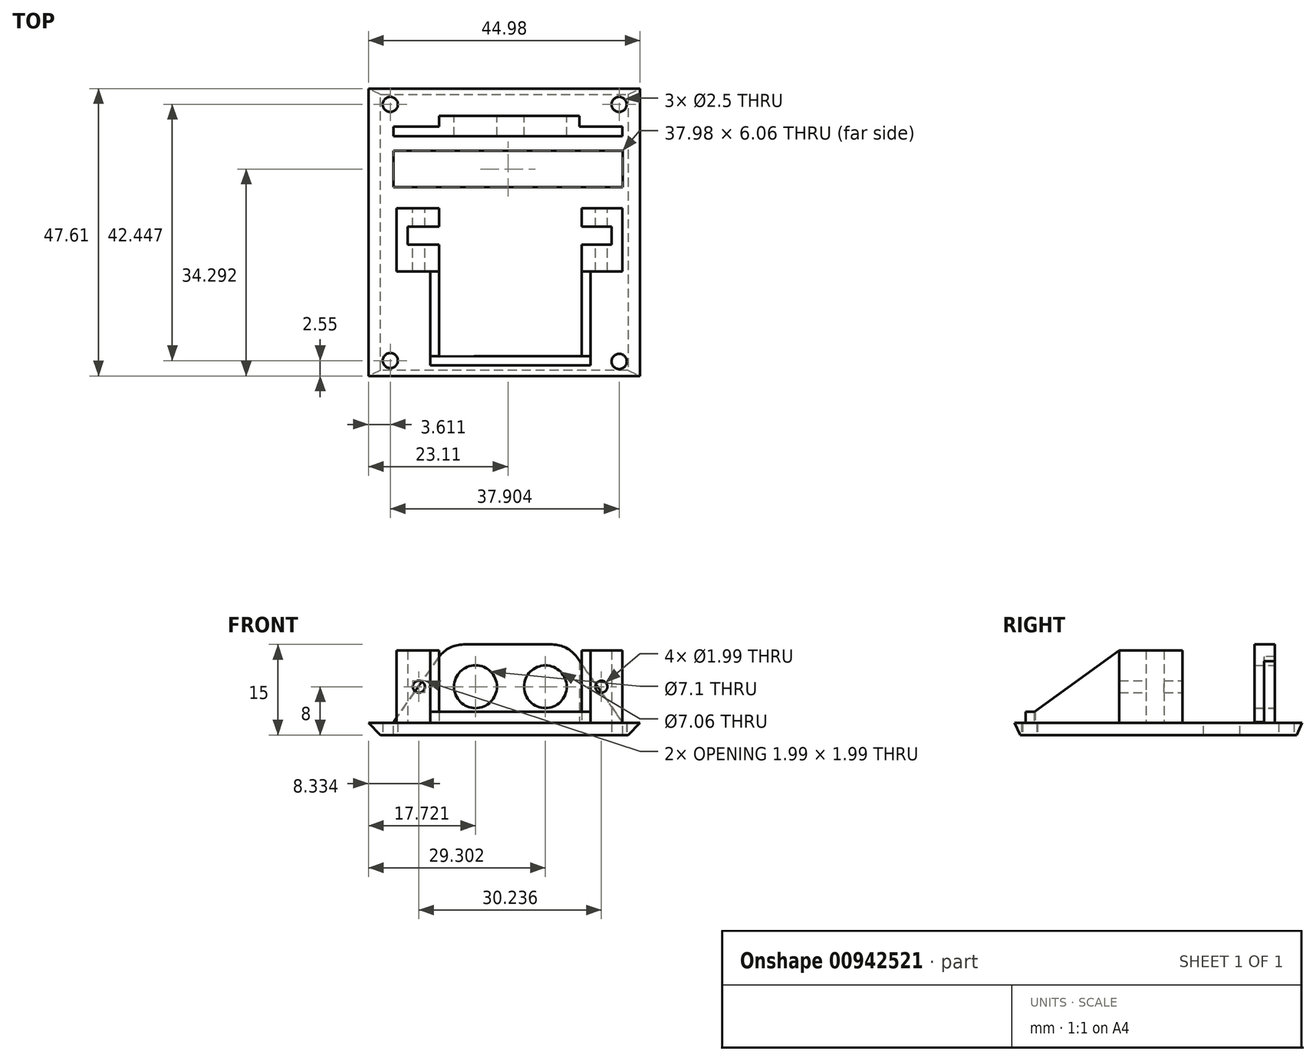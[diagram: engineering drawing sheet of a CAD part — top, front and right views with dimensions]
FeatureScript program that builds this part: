
annotation { "Feature Type Name" : "Feature", "Feature Type Description" : "" }
export const myFeature = defineFeature(function(context is Context, id is Id, definition is map)
    precondition{}
    {
        {
            var Q0;
            Q0=qCreatedBy(makeId("Top.planeOp"),FACE);
            var sketch = newSketch(context, id + "F0", { "sketchPlane" : qUnion([Q0])});
            skLineSegment(sketch, "E0.bottom", {"start": v(0, 0) * mm, "end": v(-44.98, 0) * mm});
            skLineSegment(sketch, "E0.top", {"start": v(0, 49.75) * mm, "end": v(-44.98, 49.75) * mm});
            skLineSegment(sketch, "E0.left", {"start": v(0, 0) * mm, "end": v(0, 49.75) * mm});
            skLineSegment(sketch, "E0.right", {"start": v(-44.98, 0) * mm, "end": v(-44.98, 49.75) * mm});
            skSolve(sketch);
        }
        {
            var Q0;
            Q0=makeQuery(id+"F0.imprint","IMPRINT",FACE,{"disambiguationData":[TD([[makeQuery(id+"F0.imprint","IMPRINT",EDGE,{"derivedFrom":sQuery(id+"F0.wireOp",EDGE,"E0.bottom")}),-1.0]])]});
            var sketch = newSketch(context, id + "F1", { "sketchPlane" : qUnion([Q0])});
            skLineSegment(sketch, "E1", {"start": v(-9.68, 4.44) * mm, "end": v(-9.68, 22.8) * mm});
            skLineSegment(sketch, "E2", {"start": v(-9.68, 22.8) * mm, "end": v(-4.7, 22.8) * mm});
            skLineSegment(sketch, "E3", {"start": v(-4.7, 22.8) * mm, "end": v(-4.7, 25.8) * mm});
            skLineSegment(sketch, "E4", {"start": v(-4.7, 25.8) * mm, "end": v(-9.68, 25.8) * mm});
            skLineSegment(sketch, "E5", {"start": v(-9.68, 25.8) * mm, "end": v(-9.68, 28.87) * mm});
            skLineSegment(sketch, "E6", {"start": v(-9.68, 28.87) * mm, "end": v(-2.9, 28.87) * mm});
            skLineSegment(sketch, "E7", {"start": v(-2.9, 28.87) * mm, "end": v(-2.9, 18.4) * mm});
            skLineSegment(sketch, "E8", {"start": v(-2.9, 18.4) * mm, "end": v(-8.18, 18.4) * mm});
            skLineSegment(sketch, "E9", {"start": v(-8.18, 18.4) * mm, "end": v(-8.18, 2.84) * mm});
            skLineSegment(sketch, "E10", {"start": v(-8.18, 2.84) * mm, "end": v(-34.77, 2.84) * mm});
            skLineSegment(sketch, "E11", {"start": v(-34.77, 2.84) * mm, "end": v(-34.77, 18.4) * mm});
            skLineSegment(sketch, "E12", {"start": v(-34.77, 18.4) * mm, "end": v(-40.33, 18.4) * mm});
            skLineSegment(sketch, "E13", {"start": v(-40.33, 18.4) * mm, "end": v(-40.33, 28.87) * mm});
            skLineSegment(sketch, "E14", {"start": v(-40.33, 28.87) * mm, "end": v(-33.26, 28.87) * mm});
            skLineSegment(sketch, "E15", {"start": v(-33.26, 28.87) * mm, "end": v(-33.26, 25.8) * mm});
            skLineSegment(sketch, "E16", {"start": v(-33.26, 25.8) * mm, "end": v(-38.5, 25.8) * mm});
            skLineSegment(sketch, "E17", {"start": v(-38.5, 25.8) * mm, "end": v(-38.5, 22.8) * mm});
            skLineSegment(sketch, "E18", {"start": v(-38.5, 22.8) * mm, "end": v(-33.26, 22.8) * mm});
            skLineSegment(sketch, "E19", {"start": v(-33.26, 22.8) * mm, "end": v(-33.26, 4.3) * mm});
            skLineSegment(sketch, "E20", {"start": v(-33.26, 4.3) * mm, "end": v(-9.68, 4.44) * mm});
            skLineSegment(sketch, "E21", {"start": v(-40.84, 40.8) * mm, "end": v(-2.94, 40.8) * mm});
            skLineSegment(sketch, "E22", {"start": v(-2.94, 40.8) * mm, "end": v(-2.94, 42.4) * mm});
            skLineSegment(sketch, "E23", {"start": v(-2.94, 42.4) * mm, "end": v(-10.02, 42.4) * mm});
            skLineSegment(sketch, "E24", {"start": v(-10.02, 42.4) * mm, "end": v(-10.02, 44.17) * mm});
            skLineSegment(sketch, "E25", {"start": v(-10.02, 44.17) * mm, "end": v(-33.26, 44.17) * mm});
            skLineSegment(sketch, "E26", {"start": v(-33.26, 44.17) * mm, "end": v(-33.26, 42.4) * mm});
            skLineSegment(sketch, "E27", {"start": v(-33.26, 42.4) * mm, "end": v(-40.84, 42.4) * mm});
            skLineSegment(sketch, "E28", {"start": v(-40.84, 42.4) * mm, "end": v(-40.84, 40.8) * mm});
            skSolve(sketch);
        }
        {
            var Q0;
            Q0=qCreatedBy(makeId("Top.planeOp"),FACE);
            var sketch = newSketch(context, id + "F2", { "sketchPlane" : qUnion([Q0])});
            skLineSegment(sketch, "E29.bottom", {"start": v(-40.86, 38.4) * mm, "end": v(-2.88, 38.4) * mm});
            skLineSegment(sketch, "E29.top", {"start": v(-40.86, 32.33) * mm, "end": v(-2.88, 32.33) * mm});
            skLineSegment(sketch, "E29.left", {"start": v(-40.86, 38.4) * mm, "end": v(-40.86, 32.33) * mm});
            skLineSegment(sketch, "E29.right", {"start": v(-2.88, 38.4) * mm, "end": v(-2.88, 32.33) * mm});
            skSolve(sketch);
        }
        {
            var Q0;
            Q0 = qSketchRegion(id + "F0", true);
            extrude(context, id + "F3", {"entities" : qUnion([Q0]), "oppositeDirection" : true, "depth" : 2 * mm, "offsetDistance" : 25 * mm});
        }
        {
            var Q0;
            Q0=makeQuery(id+"F1.imprint","IMPRINT",FACE,{"disambiguationData":[TD([[makeQuery(id+"F1.imprint","IMPRINT",EDGE,{"derivedFrom":sQuery(id+"F1.wireOp",EDGE,"E1")}),-1.0]])]});
            extrude(context, id + "F4", {"entities" : qUnion([Q0]), "operationType" : NewBodyOperationType.ADD, "depth" : 12 * mm, "offsetDistance" : 25 * mm});
        }
        {
            var Q0;
            Q0 = qSketchRegion(id + "F2", true);
            extrude(context, id + "F5", {"entities" : qUnion([Q0]), "operationType" : NewBodyOperationType.REMOVE, "oppositeDirection" : true, "depth" : 6.6 * mm, "offsetDistance" : 25 * mm});
        }
        {
            var Q0;
            Q0=makeQuery(id+"F1.imprint","IMPRINT",FACE,{"disambiguationData":[TD([[makeQuery(id+"F1.imprint","IMPRINT",EDGE,{"derivedFrom":sQuery(id+"F1.wireOp",EDGE,"E21")}),1.0]])]});
            extrude(context, id + "F6", {"entities" : qUnion([Q0]), "operationType" : NewBodyOperationType.ADD, "depth" : 13 * mm, "offsetDistance" : 25 * mm});
        }
        {
            var Q0;
            Q0=makeQuery(id+"F6.opExtrude","SWEPT_FACE",FACE,{"disambiguationData":[OSD([sQuery(id+"F1.wireOp",EDGE,"E25")])]});
            var sketch = newSketch(context, id + "F7", { "sketchPlane" : qUnion([Q0])});
            skCircle(sketch, "E30", {"center": v(15.68, 6) * mm, "radius": 3.53 * mm});
            skCircle(sketch, "E31", {"center": v(27.26, 6) * mm, "radius": 3.55 * mm});
            skSolve(sketch);
        }
        {
            var Q0;
            Q0 = qSketchRegion(id + "F7", true);
            extrude(context, id + "F8", {"entities" : qUnion([Q0]), "operationType" : NewBodyOperationType.REMOVE, "oppositeDirection" : true, "depth" : 5 * mm, "offsetDistance" : 25 * mm});
        }
        {
            var Q0;
            Q0=makeQuery(id+"F6.opExtrude","CAP_EDGE",EDGE,{"disambiguationData":[OSD([sQuery(id+"F1.wireOp",EDGE,"E28")])],"isStart":false});
            var Q1;
            Q1=makeQuery(id+"F6.opExtrude","CAP_EDGE",EDGE,{"disambiguationData":[OSD([sQuery(id+"F1.wireOp",EDGE,"E22")])],"isStart":false});
            chamfer(context, id + "F9", {"entities" : qUnion([Q0, Q1]), "chamferType" : ChamferType.OFFSET_ANGLE, "width" : 9 * mm, "oppositeDirection" : false, "angle" : 55 * degree, "tangentPropagation" : true});
        }
        {
            var Q0;
            {var subQ0=sQuery(id+"F1.wireOp",EDGE,"E22");Q0=makeQuery(id+"F9.opChamfer","BLEND_EDGE",EDGE,{"blendedFrom":[makeQuery(id+"F6.opExtrude","CAP_EDGE",EDGE,{"disambiguationData":[OSD([subQ0])],"isStart":false}),makeQuery(id+"F6.opExtrude","CAP_FACE",FACE,{"disambiguationData":[OSD([sQuery(id+"F1.wireOp",EDGE,"E21"),subQ0,sQuery(id+"F1.wireOp",EDGE,"E23"),sQuery(id+"F1.wireOp",EDGE,"E24"),sQuery(id+"F1.wireOp",EDGE,"E25"),sQuery(id+"F1.wireOp",EDGE,"E26"),sQuery(id+"F1.wireOp",EDGE,"E27"),sQuery(id+"F1.wireOp",EDGE,"E28")])],"isStart":false})],"blendedInto":[makeQuery(id+"F6.opExtrude","CAP_FACE",FACE,{"disambiguationData":[OSD([sQuery(id+"F1.wireOp",EDGE,"E21"),subQ0,sQuery(id+"F1.wireOp",EDGE,"E23"),sQuery(id+"F1.wireOp",EDGE,"E24"),sQuery(id+"F1.wireOp",EDGE,"E25"),sQuery(id+"F1.wireOp",EDGE,"E26"),sQuery(id+"F1.wireOp",EDGE,"E27"),sQuery(id+"F1.wireOp",EDGE,"E28")])],"isStart":false})]});}
            var Q1;
            {var subQ0=sQuery(id+"F1.wireOp",EDGE,"E28");Q1=makeQuery(id+"F9.opChamfer","BLEND_EDGE",EDGE,{"blendedFrom":[makeQuery(id+"F6.opExtrude","CAP_EDGE",EDGE,{"disambiguationData":[OSD([subQ0])],"isStart":false}),makeQuery(id+"F6.opExtrude","CAP_FACE",FACE,{"disambiguationData":[OSD([sQuery(id+"F1.wireOp",EDGE,"E21"),sQuery(id+"F1.wireOp",EDGE,"E22"),sQuery(id+"F1.wireOp",EDGE,"E23"),sQuery(id+"F1.wireOp",EDGE,"E24"),sQuery(id+"F1.wireOp",EDGE,"E25"),sQuery(id+"F1.wireOp",EDGE,"E26"),sQuery(id+"F1.wireOp",EDGE,"E27"),subQ0])],"isStart":false})],"blendedInto":[makeQuery(id+"F6.opExtrude","CAP_FACE",FACE,{"disambiguationData":[OSD([sQuery(id+"F1.wireOp",EDGE,"E21"),sQuery(id+"F1.wireOp",EDGE,"E22"),sQuery(id+"F1.wireOp",EDGE,"E23"),sQuery(id+"F1.wireOp",EDGE,"E24"),sQuery(id+"F1.wireOp",EDGE,"E25"),sQuery(id+"F1.wireOp",EDGE,"E26"),sQuery(id+"F1.wireOp",EDGE,"E27"),subQ0])],"isStart":false})]});}
            fillet(context, id + "F10", {"entities" : qUnion([Q0, Q1]), "radius" : 5 * mm, "tangentPropagation" : true, "allowEdgeOverflow" : false});
        }
        {
            var Q0;
            Q0=makeQuery(id+"F4.opExtrude","SWEPT_FACE",FACE,{"disambiguationData":[OSD([sQuery(id+"F1.wireOp",EDGE,"E6")])]});
            var sketch = newSketch(context, id + "F11", { "sketchPlane" : qUnion([Q0])});
            skCircle(sketch, "E32", {"center": v(6.41, 6) * mm, "radius": 1 * mm});
            skPoint(sketch, "E32.centerSnap0", {"position": v(9.68, 6) * mm});
            skSolve(sketch);
        }
        {
            var Q0;
            Q0 = qSketchRegion(id + "F11", true);
            extrude(context, id + "F12", {"entities" : qUnion([Q0]), "operationType" : NewBodyOperationType.REMOVE, "oppositeDirection" : true, "depth" : 11 * mm, "offsetDistance" : 25 * mm});
        }
        {
            var Q0;
            Q0=makeQuery(id+"F4.opExtrude","SWEPT_FACE",FACE,{"disambiguationData":[OSD([sQuery(id+"F1.wireOp",EDGE,"E14")])]});
            var sketch = newSketch(context, id + "F13", { "sketchPlane" : qUnion([Q0])});
            skCircle(sketch, "E33", {"center": v(36.65, 6) * mm, "radius": 1 * mm});
            skPoint(sketch, "E33.centerSnap0", {"position": v(40.33, 6) * mm});
            skSolve(sketch);
        }
        {
            var Q0;
            Q0 = qSketchRegion(id + "F13", true);
            extrude(context, id + "F14", {"entities" : qUnion([Q0]), "operationType" : NewBodyOperationType.REMOVE, "oppositeDirection" : true, "depth" : 11 * mm, "offsetDistance" : 25 * mm});
        }
        {
            var Q0;
            Q0=makeQuery(id+"F3.opExtrude","CAP_FACE",FACE,{"disambiguationData":[OSD([sQuery(id+"F0.wireOp",EDGE,"E0.bottom"),sQuery(id+"F0.wireOp",EDGE,"E0.top"),sQuery(id+"F0.wireOp",EDGE,"E0.left"),sQuery(id+"F0.wireOp",EDGE,"E0.right")])],"isStart":false});
            var sketch = newSketch(context, id + "F15", { "sketchPlane" : qUnion([Q0])});
            skCircle(sketch, "E34", {"center": v(-41.37, -3.62) * mm, "radius": 1.25 * mm});
            skCircle(sketch, "E35", {"center": v(-3.47, -3.46) * mm, "radius": 1.26 * mm});
            skCircle(sketch, "E36", {"center": v(-41.37, -46.07) * mm, "radius": 1.25 * mm});
            skCircle(sketch, "E37", {"center": v(-3.47, -46.07) * mm, "radius": 1.25 * mm});
            skSolve(sketch);
        }
        {
            var Q0;
            Q0 = qSketchRegion(id + "F15", true);
            extrude(context, id + "F16", {"entities" : qUnion([Q0]), "operationType" : NewBodyOperationType.REMOVE, "oppositeDirection" : true, "depth" : 4 * mm, "offsetDistance" : 25 * mm});
        }
        {
            var Q0;
            Q0=makeQuery(id+"F4.opExtrude","SWEPT_FACE",FACE,{"disambiguationData":[OSD([sQuery(id+"F1.wireOp",EDGE,"E11")])]});
            var sketch = newSketch(context, id + "F17", { "sketchPlane" : qUnion([Q0])});
            skLineSegment(sketch, "E38", {"start": v(-18.4, 12) * mm, "end": v(-4.33, 1.85) * mm});
            skLineSegment(sketch, "E39", {"start": v(-4.33, 1.85) * mm, "end": v(-2.84, 1.85) * mm});
            skLineSegment(sketch, "E40", {"start": v(-2.84, 1.85) * mm, "end": v(-2.84, 12) * mm});
            skLineSegment(sketch, "E41", {"start": v(-2.84, 12) * mm, "end": v(-18.4, 12) * mm});
            skSolve(sketch);
        }
        {
            var Q0;
            Q0 = qSketchRegion(id + "F17", true);
            extrude(context, id + "F18", {"entities" : qUnion([Q0]), "operationType" : NewBodyOperationType.REMOVE, "oppositeDirection" : true, "depth" : 29.1 * mm, "offsetDistance" : 25 * mm});
        }
        {
            var Q0;
            Q0=makeQuery(id+"F3.opExtrude","CAP_EDGE",EDGE,{"disambiguationData":[OSD([sQuery(id+"F0.wireOp",EDGE,"E0.right")])],"isStart":false});
            var Q1;
            Q1=makeQuery(id+"F3.opExtrude","CAP_EDGE",EDGE,{"disambiguationData":[OSD([sQuery(id+"F0.wireOp",EDGE,"E0.left")])],"isStart":false});
            chamfer(context, id + "F19", {"entities" : qUnion([Q0, Q1]), "width" : 2 * mm, "tangentPropagation" : true});
        }
        {
            var Q0;
            Q0=makeQuery(id+"F3.opExtrude","CAP_EDGE",EDGE,{"disambiguationData":[OSD([sQuery(id+"F0.wireOp",EDGE,"E0.bottom")])],"isStart":false});
            var Q1;
            Q1=makeQuery(id+"F3.opExtrude","CAP_EDGE",EDGE,{"disambiguationData":[OSD([sQuery(id+"F0.wireOp",EDGE,"E0.top")])],"isStart":false});
            chamfer(context, id + "F20", {"entities" : qUnion([Q0, Q1]), "chamferType" : ChamferType.OFFSET_ANGLE, "width" : 2 * mm, "oppositeDirection" : false, "angle" : 65 * degree, "tangentPropagation" : true});
        }
    });
